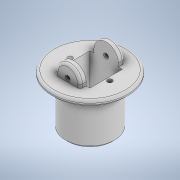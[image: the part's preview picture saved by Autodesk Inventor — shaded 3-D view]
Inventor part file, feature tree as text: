
AUTODESK INVENTOR PART (.ipt)
format: ipt  version: 2022 (Build 260153000, 153)  size: 210,944 bytes
history: native  units: in
note: dims shown in document units (in); Inventor stores cm internally (conversion verified against a paired STEP export)
features: extrude x6, sketch x6, chamfer x2, fillet x2
ambient origin geometry x8: Origin, YZ Plane, XZ Plane, XY Plane, X Axis, Y Axis, Z Axis, Center Point
bodies: Solid1 (feature_tree)
feature tree (16):
  extrude  "Extrusion1"  Depth=1.4567in TaperAngle=0.0deg
  extrude  "Extrusion2"  Depth=0.1969in TaperAngle=0.0deg
  chamfer  "Chamfer1"  Distance=0.0787in Angle=45.0deg
  extrude  "Extrusion3"  Depth=1.0394in
  extrude  "Extrusion4"  Depth=0.1575in
  extrude  "Extrusion5"  Depth=0.7874in TaperAngle=0.0deg
  fillet  "Fillet1"  Radius=0.7874in
  extrude  "Extrusion6"  Depth=0.7874in
  fillet  "Fillet2"  Radius=0.1969in
  chamfer  "Chamfer2"  Distance=0.5079in
  sketch  "Sketch1"  dims[d0=1.5748in d1=1.4567in d2=0.0in]
  sketch  "Sketch2"  dims[d3=2.4409in d4=0.1969in d5=0.0in d6=0.0787in d7=0.0787in d8=45.0deg]
  sketch  "Sketch3"  dims[d9=1.0394in d10=1.0394in]
  sketch  "Sketch4"  dims[d11=1.9685in d12=0.0in d13=0.1575in]
  sketch  "Sketch5"  dims[d14=0.1575in d15=1.9685in d16=0.0in d17=0.7874in]
  sketch  "Sketch6"  dims[d18=0.1969in d19=0.7874in d20=0.1969in d21=0.5079in d22=0.0in d23=0.3937in d24=0.1575in d25=1.9685in d26=0.0in d27=0.0787in d28=0.0787in d29=0.0787in d30=45.0deg]
